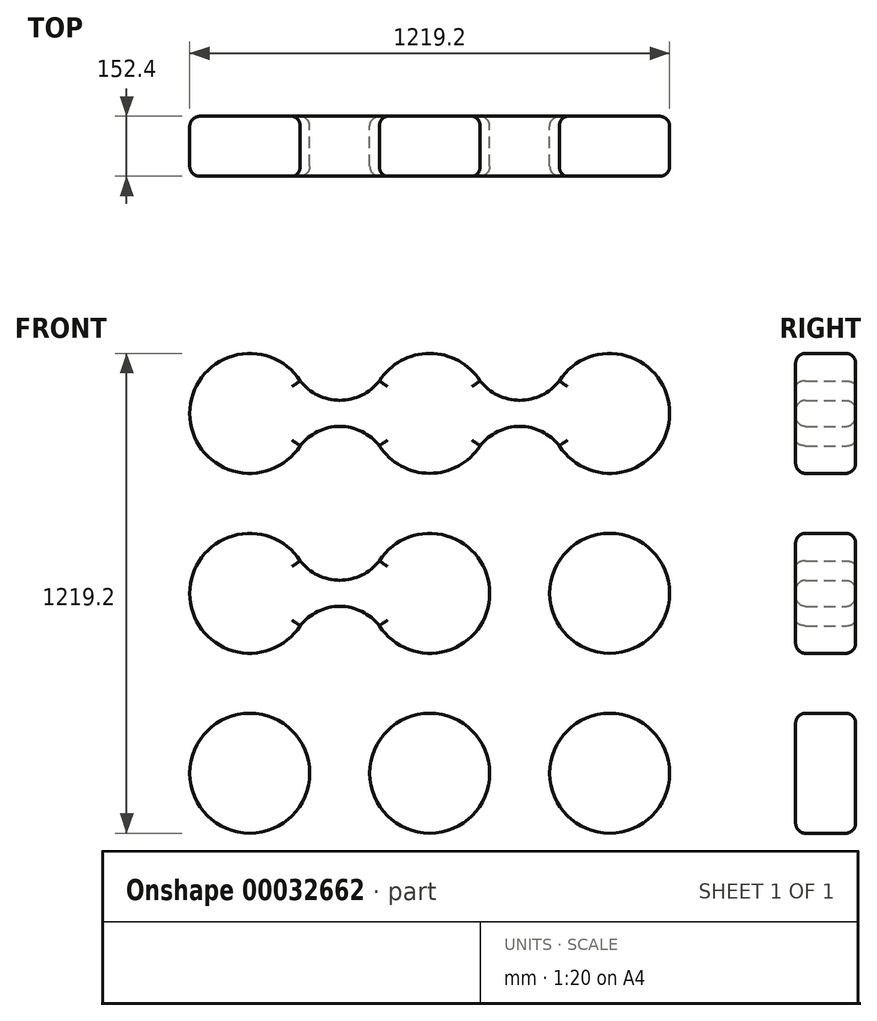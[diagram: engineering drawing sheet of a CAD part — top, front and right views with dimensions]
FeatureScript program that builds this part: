
annotation { "Feature Type Name" : "Feature", "Feature Type Description" : "" }
export const myFeature = defineFeature(function(context is Context, id is Id, definition is map)
    precondition{}
    {
        {
            var Q0;
            Q0=qCreatedBy(makeId("Front.planeOp"),FACE);
            var sketch = newSketch(context, id + "F0", { "sketchPlane" : qUnion([Q0])});
            skArc(sketch, "E0", {"start": v(-128.1, -82.55) * mm, "mid": v(152.4, 0) * mm, "end": v(-128.1, 82.55) * mm});
            skLineSegment(sketch, "E1", {"start": v(0, 0) * mm, "end": v(457.2, 0) * mm, "construction": true});
            skLineSegment(sketch, "E2", {"start": v(0, 0) * mm, "end": v(-457.2, 0) * mm, "construction": true});
            skCircle(sketch, "E3", {"center": v(457.2, 0) * mm, "radius": 152.4 * mm});
            skArc(sketch, "E4", {"start": v(-329.1, 82.55) * mm, "mid": v(-609.6, 0) * mm, "end": v(-329.1, -82.55) * mm});
            skLineSegment(sketch, "E5", {"start": v(457.2, 0) * mm, "end": v(457.2, -457.2) * mm, "construction": true});
            skCircle(sketch, "E6", {"center": v(457.2, -457.2) * mm, "radius": 152.4 * mm});
            skLineSegment(sketch, "E7", {"start": v(457.2, -457.2) * mm, "end": v(0, -457.2) * mm, "construction": true});
            skLineSegment(sketch, "E8", {"start": v(0, -457.2) * mm, "end": v(-457.2, -457.2) * mm, "construction": true});
            skCircle(sketch, "E9", {"center": v(0, -457.2) * mm, "radius": 152.4 * mm});
            skCircle(sketch, "E10", {"center": v(-457.2, -457.2) * mm, "radius": 152.4 * mm});
            skLineSegment(sketch, "E11", {"start": v(457.2, 0) * mm, "end": v(457.2, 457.2) * mm, "construction": true});
            skLineSegment(sketch, "E12", {"start": v(457.2, 457.2) * mm, "end": v(0, 457.2) * mm, "construction": true});
            skLineSegment(sketch, "E13", {"start": v(0, 457.2) * mm, "end": v(-457.2, 457.2) * mm, "construction": true});
            skArc(sketch, "E14", {"start": v(-329.1, 539.75) * mm, "mid": v(-609.6, 457.2) * mm, "end": v(-329.1, 374.65) * mm});
            skArc(sketch, "E15", {"start": v(-128.1, 374.65) * mm, "mid": v(0, 304.8) * mm, "end": v(128.1, 374.65) * mm});
            skArc(sketch, "E16", {"start": v(329.1, 374.65) * mm, "mid": v(609.6, 457.2) * mm, "end": v(329.1, 539.75) * mm});
            skLineSegment(sketch, "E17.0", {"start": v(-128.1, 82.55) * mm, "end": v(-329.1, 82.55) * mm, "construction": true});
            skArc(sketch, "E18", {"start": v(-329.1, 82.55) * mm, "mid": v(-228.6, 33.2) * mm, "end": v(-128.1, 82.55) * mm});
            skArc(sketch, "E19.MirrorCS", {"start": v(-329.1, -82.55) * mm, "mid": v(-228.6, -33.2) * mm, "end": v(-128.1, -82.55) * mm});
            skLineSegment(sketch, "E20.0", {"start": v(-128.1, 539.75) * mm, "end": v(-329.1, 539.75) * mm, "construction": true});
            skLineSegment(sketch, "E21.0", {"start": v(329.1, 539.75) * mm, "end": v(128.1, 539.75) * mm, "construction": true});
            skArc(sketch, "E22", {"start": v(-329.1, 539.75) * mm, "mid": v(-228.6, 490.4) * mm, "end": v(-128.1, 539.75) * mm});
            skArc(sketch, "E23", {"start": v(128.1, 539.75) * mm, "mid": v(228.6, 490.4) * mm, "end": v(329.1, 539.75) * mm});
            skArc(sketch, "E24.MirrorCS", {"start": v(128.1, 374.65) * mm, "mid": v(228.6, 424) * mm, "end": v(329.1, 374.65) * mm});
            skArc(sketch, "E25.MirrorCS", {"start": v(-329.1, 374.65) * mm, "mid": v(-228.6, 424) * mm, "end": v(-128.1, 374.65) * mm});
            skArc(sketch, "E26.trimOffspring", {"start": v(128.1, 539.75) * mm, "mid": v(0, 609.6) * mm, "end": v(-128.1, 539.75) * mm});
            skSolve(sketch);
        }
        {
            var Q0;
            Q0=makeQuery(id+"F0.imprint","IMPRINT",FACE,{"disambiguationData":[TD([[makeQuery(id+"F0.imprint","IMPRINT",EDGE,{"derivedFrom":sQuery(id+"F0.wireOp",EDGE,"E14")}),1.0]])]});
            var Q1;
            Q1=makeQuery(id+"F0.imprint","IMPRINT",FACE,{"disambiguationData":[TD([[makeQuery(id+"F0.imprint","IMPRINT",EDGE,{"derivedFrom":sQuery(id+"F0.wireOp",EDGE,"E0")}),1.0]])]});
            var Q2;
            Q2=makeQuery(id+"F0.imprint","IMPRINT",FACE,{"disambiguationData":[TD([[makeQuery(id+"F0.imprint","IMPRINT",EDGE,{"derivedFrom":sQuery(id+"F0.wireOp",EDGE,"E3")}),1.0]])]});
            var Q3;
            Q3=makeQuery(id+"F0.imprint","IMPRINT",FACE,{"disambiguationData":[TD([[makeQuery(id+"F0.imprint","IMPRINT",EDGE,{"derivedFrom":sQuery(id+"F0.wireOp",EDGE,"E6")}),1.0]])]});
            var Q4;
            Q4=makeQuery(id+"F0.imprint","IMPRINT",FACE,{"disambiguationData":[TD([[makeQuery(id+"F0.imprint","IMPRINT",EDGE,{"derivedFrom":sQuery(id+"F0.wireOp",EDGE,"E9")}),1.0]])]});
            var Q5;
            Q5=makeQuery(id+"F0.imprint","IMPRINT",FACE,{"disambiguationData":[TD([[makeQuery(id+"F0.imprint","IMPRINT",EDGE,{"derivedFrom":sQuery(id+"F0.wireOp",EDGE,"E10")}),1.0]])]});
            extrude(context, id + "F1", {"entities" : qUnion([Q0, Q1, Q2, Q3, Q4, Q5]), "depth" : 152.4 * mm});
        }
        {
            var Q0;
            Q0=makeQuery(id+"F1.opExtrude","SWEPT_FACE",FACE,{"disambiguationData":[OSD([sQuery(id+"F0.wireOp",EDGE,"E10")])]});
            var Q1;
            Q1=makeQuery(id+"F1.opExtrude","SWEPT_FACE",FACE,{"disambiguationData":[OSD([sQuery(id+"F0.wireOp",EDGE,"E9")])]});
            var Q2;
            Q2=makeQuery(id+"F1.opExtrude","SWEPT_FACE",FACE,{"disambiguationData":[OSD([sQuery(id+"F0.wireOp",EDGE,"E6")])]});
            var Q3;
            Q3=makeQuery(id+"F1.opExtrude","SWEPT_FACE",FACE,{"disambiguationData":[OSD([sQuery(id+"F0.wireOp",EDGE,"E3")])]});
            fillet(context, id + "F2", {"entities" : qUnion([Q0, Q1, Q2, Q3]), "radius" : 25.4 * mm, "tangentPropagation" : true, "allowEdgeOverflow" : false});
        }
        {
            var Q0;
            Q0=makeQuery(id+"F1.opExtrude","CAP_FACE",FACE,{"disambiguationData":[OSD([sQuery(id+"F0.wireOp",EDGE,"E14"),sQuery(id+"F0.wireOp",EDGE,"E15"),sQuery(id+"F0.wireOp",EDGE,"E16"),sQuery(id+"F0.wireOp",EDGE,"E22"),sQuery(id+"F0.wireOp",EDGE,"E23"),sQuery(id+"F0.wireOp",EDGE,"E24.MirrorCS"),sQuery(id+"F0.wireOp",EDGE,"E25.MirrorCS"),sQuery(id+"F0.wireOp",EDGE,"E26.trimOffspring")])],"isStart":false});
            var Q1;
            Q1=makeQuery(id+"F1.opExtrude","CAP_FACE",FACE,{"disambiguationData":[OSD([sQuery(id+"F0.wireOp",EDGE,"E0"),sQuery(id+"F0.wireOp",EDGE,"E4"),sQuery(id+"F0.wireOp",EDGE,"E18"),sQuery(id+"F0.wireOp",EDGE,"E19.MirrorCS")])],"isStart":false});
            var Q2;
            Q2=makeQuery(id+"F1.opExtrude","CAP_FACE",FACE,{"disambiguationData":[OSD([sQuery(id+"F0.wireOp",EDGE,"E0"),sQuery(id+"F0.wireOp",EDGE,"E4"),sQuery(id+"F0.wireOp",EDGE,"E18"),sQuery(id+"F0.wireOp",EDGE,"E19.MirrorCS")])],"isStart":true});
            var Q3;
            Q3=makeQuery(id+"F1.opExtrude","CAP_FACE",FACE,{"disambiguationData":[OSD([sQuery(id+"F0.wireOp",EDGE,"E14"),sQuery(id+"F0.wireOp",EDGE,"E15"),sQuery(id+"F0.wireOp",EDGE,"E16"),sQuery(id+"F0.wireOp",EDGE,"E22"),sQuery(id+"F0.wireOp",EDGE,"E23"),sQuery(id+"F0.wireOp",EDGE,"E24.MirrorCS"),sQuery(id+"F0.wireOp",EDGE,"E25.MirrorCS"),sQuery(id+"F0.wireOp",EDGE,"E26.trimOffspring")])],"isStart":true});
            fillet(context, id + "F3", {"entities" : qUnion([Q0, Q1, Q2, Q3]), "radius" : 25.4 * mm, "tangentPropagation" : true, "allowEdgeOverflow" : false});
        }
    });
